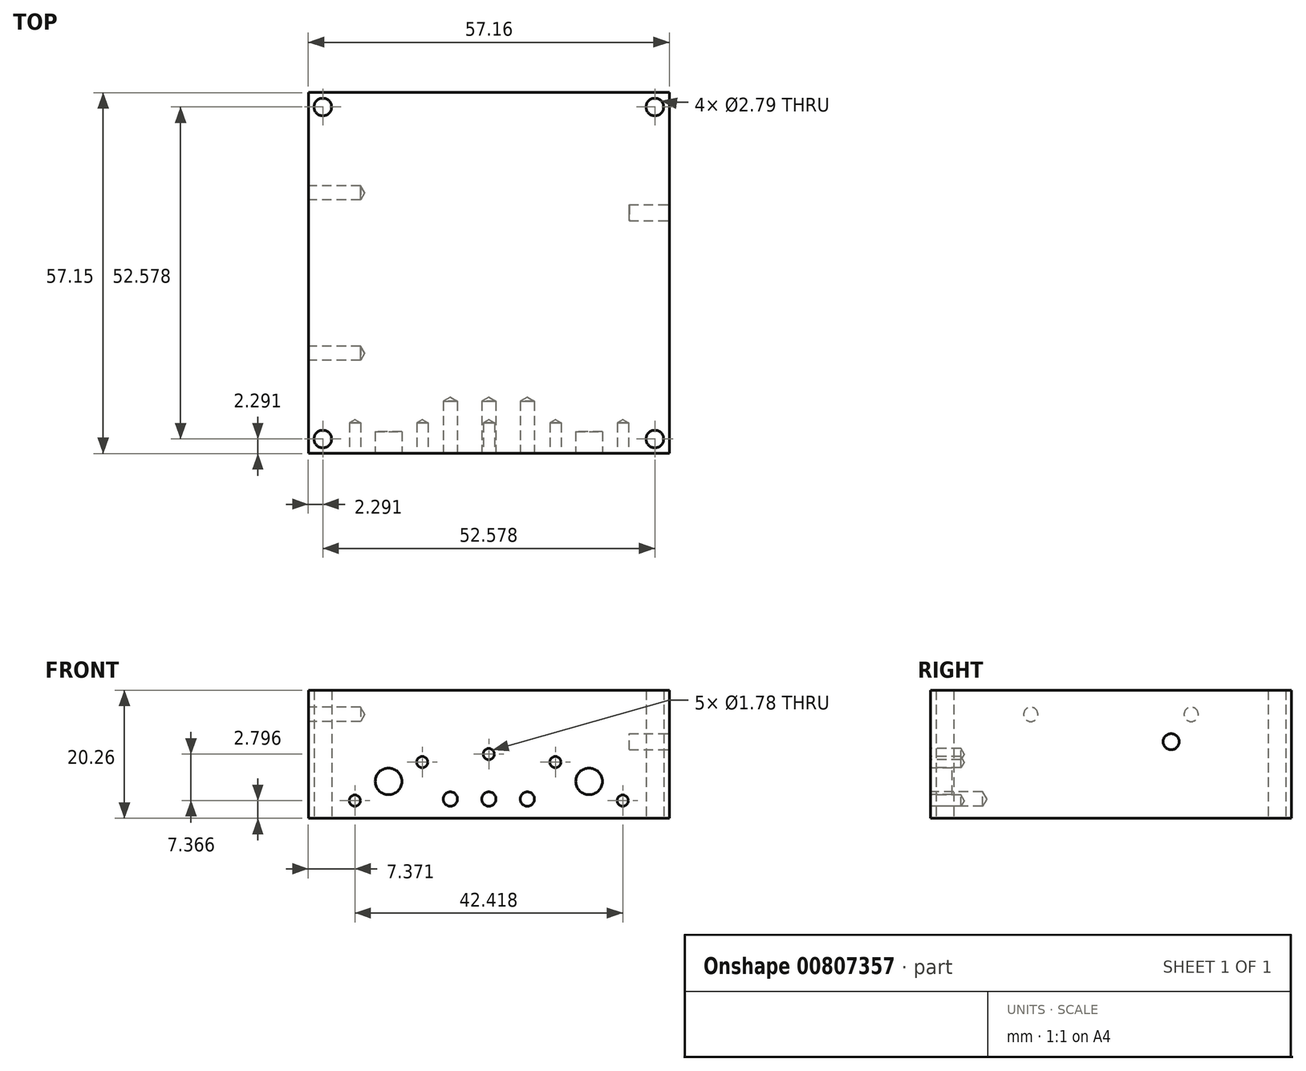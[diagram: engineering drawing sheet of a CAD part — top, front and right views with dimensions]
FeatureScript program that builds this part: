
annotation { "Feature Type Name" : "Feature", "Feature Type Description" : "" }
export const myFeature = defineFeature(function(context is Context, id is Id, definition is map)
    precondition{}
    {
        {
            var Q0;
            Q0=qCreatedBy(makeId("Top.planeOp"),FACE);
            var sketch = newSketch(context, id + "F0", { "sketchPlane" : qUnion([Q0])});
            skLineSegment(sketch, "E0.bottom", {"start": v(-28.57, 28.57) * mm, "end": v(28.58, 28.57) * mm});
            skLineSegment(sketch, "E0.top", {"start": v(-28.58, -28.58) * mm, "end": v(28.58, -28.58) * mm});
            skLineSegment(sketch, "E0.left", {"start": v(-28.57, 28.57) * mm, "end": v(-28.58, -28.58) * mm});
            skLineSegment(sketch, "E0.right", {"start": v(28.58, 28.57) * mm, "end": v(28.58, -28.57) * mm});
            skLineSegment(sketch, "E1", {"start": v(-28.58, -28.58) * mm, "end": v(28.58, 28.58) * mm, "construction": true});
            skSolve(sketch);
        }
        {
            var Q0;
            Q0 = qSketchRegion(id + "F0", true);
            extrude(context, id + "F1", {"entities" : qUnion([Q0]), "endBound" : BoundingType.SYMMETRIC, "depth" : 20.26 * mm, "offsetDistance" : 25.4 * mm});
        }
        {
            var Q0;
            Q0=makeQuery(id+"F1.opExtrude","SWEPT_FACE",FACE,{"disambiguationData":[OSD([sQuery(id+"F0.wireOp",EDGE,"E0.top")])]});
            var sketch = newSketch(context, id + "F2", { "sketchPlane" : qUnion([Q0])});
            skCircle(sketch, "E2", {"center": v(-15.88, -4.29) * mm, "radius": 2.1 * mm});
            skCircle(sketch, "E3", {"center": v(15.88, -4.29) * mm, "radius": 2.1 * mm});
            skSolve(sketch);
        }
        {
            var Q0;
            Q0 = qSketchRegion(id + "F2", true);
            extrude(context, id + "F3", {"entities" : qUnion([Q0]), "operationType" : NewBodyOperationType.REMOVE, "oppositeDirection" : true, "depth" : 3.43 * mm, "offsetDistance" : 25.4 * mm});
        }
        {
            var Q0;
            Q0=makeQuery(id+"F1.opExtrude","SWEPT_FACE",FACE,{"disambiguationData":[OSD([sQuery(id+"F0.wireOp",EDGE,"E0.top")])]});
            var sketch = newSketch(context, id + "F4", { "sketchPlane" : qUnion([Q0])});
            skCircle(sketch, "E4", {"center": v(-21.2, -7.33) * mm, "radius": 0.18 * mm});
            skCircle(sketch, "E5", {"center": v(-10.54, -1.24) * mm, "radius": 0.18 * mm});
            skLineSegment(sketch, "E6", {"start": v(0, 10.13) * mm, "end": v(0, -10.13) * mm, "construction": true});
            skCircle(sketch, "E7.MirrorC", {"center": v(10.54, -1.24) * mm, "radius": 0.18 * mm});
            skCircle(sketch, "E8.MirrorC", {"center": v(21.2, -7.33) * mm, "radius": 0.18 * mm});
            skLineSegment(sketch, "E9", {"start": v(-15.88, -4.29) * mm, "end": v(-15.88, -10.13) * mm, "construction": true});
            skLineSegment(sketch, "E10", {"start": v(-15.88, -10.13) * mm, "end": v(-15.88, -4.29) * mm, "construction": true});
            skLineSegment(sketch, "E11", {"start": v(-28.58, -4.29) * mm, "end": v(-15.88, -4.29) * mm, "construction": true});
            skLineSegment(sketch, "E12", {"start": v(-15.91, -4.3) * mm, "end": v(-21.2, -7.33) * mm, "construction": true});
            skSolve(sketch);
        }
        {
            var Q0;
            Q0=makeQuery(id+"F1.opExtrude","CAP_FACE",FACE,{"disambiguationData":[OSD([sQuery(id+"F0.wireOp",EDGE,"E0.bottom"),sQuery(id+"F0.wireOp",EDGE,"E0.top"),sQuery(id+"F0.wireOp",EDGE,"E0.left"),sQuery(id+"F0.wireOp",EDGE,"E0.right")])],"isStart":true});
            var sketch = newSketch(context, id + "F5", { "sketchPlane" : qUnion([Q0])});
            skCircle(sketch, "E13", {"center": v(-26.29, 26.29) * mm, "radius": 1.4 * mm});
            skLineSegment(sketch, "E14", {"start": v(0, 28.58) * mm, "end": v(0, -28.57) * mm, "construction": true});
            skLineSegment(sketch, "E15", {"start": v(-28.57, 0) * mm, "end": v(28.58, 0) * mm, "construction": true});
            skCircle(sketch, "E16.MirrorC", {"center": v(26.29, 26.29) * mm, "radius": 1.4 * mm});
            skCircle(sketch, "E17.MirrorC", {"center": v(26.29, -26.29) * mm, "radius": 1.4 * mm});
            skCircle(sketch, "E18.MirrorC", {"center": v(-26.29, -26.29) * mm, "radius": 1.4 * mm});
            skSolve(sketch);
        }
        {
            var Q0;
            Q0 = qSketchRegion(id + "F5", true);
            extrude(context, id + "F6", {"entities" : qUnion([Q0]), "operationType" : NewBodyOperationType.REMOVE, "endBound" : BoundingType.THROUGH_ALL, "oppositeDirection" : true, "depth" : 25.4 * mm, "offsetDistance" : 25.4 * mm});
        }
        {
            var Q0;
            Q0=makeQuery(id+"F1.opExtrude","SWEPT_FACE",FACE,{"disambiguationData":[OSD([sQuery(id+"F0.wireOp",EDGE,"E0.left")])]});
            var sketch = newSketch(context, id + "F7", { "sketchPlane" : qUnion([Q0])});
            skPoint(sketch, "E19", {"position": v(12.7, 6.32) * mm});
            skLineSegment(sketch, "E20", {"start": v(0, 10.13) * mm, "end": v(0, -10.13) * mm, "construction": true});
            skPoint(sketch, "E21.MirrorP", {"position": v(-12.7, 6.32) * mm});
            skSolve(sketch);
        }
        {
            var Q0;
            Q0=sQuery(id+"F7.wireOp",VERTEX,"E19");
            var Q1;
            Q1=sQuery(id+"F7.wireOp",VERTEX,"E21.MirrorP");
            var Q2;
            Q2=makeQuery(id+"F1.opExtrude","SWEPT_BODY",BODY,{"disambiguationData":[OSD([sQuery(id+"F0.wireOp",EDGE,"E0.bottom"),sQuery(id+"F0.wireOp",EDGE,"E0.top"),sQuery(id+"F0.wireOp",EDGE,"E0.left"),sQuery(id+"F0.wireOp",EDGE,"E0.right")])]});
            hole(context, id + "F8", {"style" : HoleStyle.SIMPLE, "endStyle" : HoleEndStyle.BLIND, "standardTappedOrClearance" : lookupTablePath({ "standard" : "ANSI", "engagement" : "75%", "pitch" : "40 tpi", "size" : "#4", "type" : "Tapped" }), "standardBlindInLast" : lookupTablePath({ "standard" : "ANSI", "engagement" : "75%", "pitch" : "40 tpi", "size" : "#4", "type" : "Tapped" }), "holeDiameter" : 2.26 * mm, "majorDiameter" : 2.84 * mm, "showTappedDepth" : true, "holeDepth" : 8.27 * mm, "tappedDepth" : 6.36 * mm, "tapClearance" : 3, "locations" : qUnion([Q0, Q1]), "scope" : qUnion([Q2])});
        }
        {
            var Q0;
            Q0=makeQuery(id+"F1.opExtrude","SWEPT_FACE",FACE,{"disambiguationData":[OSD([sQuery(id+"F0.wireOp",EDGE,"E0.right")])]});
            var sketch = newSketch(context, id + "F9", { "sketchPlane" : qUnion([Q0])});
            skCircle(sketch, "E22", {"center": v(9.53, 2) * mm, "radius": 1.27 * mm});
            skSolve(sketch);
        }
        {
            var Q0;
            Q0 = qSketchRegion(id + "F9", true);
            extrude(context, id + "F10", {"entities" : qUnion([Q0]), "operationType" : NewBodyOperationType.REMOVE, "oppositeDirection" : true, "depth" : 6.35 * mm, "offsetDistance" : 25.4 * mm});
        }
        {
            var Q0;
            Q0=makeQuery(id+"F1.opExtrude","SWEPT_FACE",FACE,{"disambiguationData":[OSD([sQuery(id+"F0.wireOp",EDGE,"E0.top")])]});
            var sketch = newSketch(context, id + "F11", { "sketchPlane" : qUnion([Q0])});
            skPoint(sketch, "E23", {"position": v(-6.1, -7.08) * mm});
            skPoint(sketch, "E24", {"position": v(0, -7.08) * mm});
            skPoint(sketch, "E25", {"position": v(6.1, -7.08) * mm});
            skSolve(sketch);
        }
        {
            var Q0;
            Q0=sQuery(id+"F11.wireOp",VERTEX,"E23");
            var Q1;
            Q1=sQuery(id+"F11.wireOp",VERTEX,"E24");
            var Q2;
            Q2=sQuery(id+"F11.wireOp",VERTEX,"E25");
            var Q3;
            Q3=makeQuery(id+"F1.opExtrude","SWEPT_BODY",BODY,{"disambiguationData":[OSD([sQuery(id+"F0.wireOp",EDGE,"E0.bottom"),sQuery(id+"F0.wireOp",EDGE,"E0.top"),sQuery(id+"F0.wireOp",EDGE,"E0.left"),sQuery(id+"F0.wireOp",EDGE,"E0.right")])]});
            hole(context, id + "F12", {"style" : HoleStyle.SIMPLE, "endStyle" : HoleEndStyle.BLIND, "standardTappedOrClearance" : lookupTablePath({ "standard" : "ANSI", "engagement" : "75%", "pitch" : "40 tpi", "size" : "#4", "type" : "Tapped" }), "standardBlindInLast" : lookupTablePath({ "standard" : "ANSI", "engagement" : "75%", "pitch" : "40 tpi", "size" : "#4", "type" : "Tapped" }), "holeDiameter" : 2.26 * mm, "majorDiameter" : 2.84 * mm, "showTappedDepth" : true, "holeDepth" : 8.26 * mm, "isTappedThrough" : true, "tappedDepth" : 6.35 * mm, "tapClearance" : 3, "locations" : qUnion([Q0, Q1, Q2]), "scope" : qUnion([Q3])});
        }
        {
            var Q0;
            Q0=makeQuery(id+"F1.opExtrude","SWEPT_FACE",FACE,{"disambiguationData":[OSD([sQuery(id+"F0.wireOp",EDGE,"E0.top")])]});
            var sketch = newSketch(context, id + "F13", { "sketchPlane" : qUnion([Q0])});
            skPoint(sketch, "E26", {"position": v(0, 0.03) * mm});
            skSolve(sketch);
        }
        {
            var Q0;
            Q0=sQuery(id+"F4.wireOp",VERTEX,"E12.end");
            var Q1;
            Q1=sQuery(id+"F4.wireOp",VERTEX,"E5.center");
            var Q2;
            Q2=sQuery(id+"F4.wireOp",VERTEX,"E7.MirrorC.center");
            var Q3;
            Q3=sQuery(id+"F4.wireOp",VERTEX,"E8.MirrorC.center");
            var Q4;
            Q4=sQuery(id+"F13.wireOp",VERTEX,"E26");
            var Q5;
            Q5=makeQuery(id+"F1.opExtrude","SWEPT_BODY",BODY,{"disambiguationData":[OSD([sQuery(id+"F0.wireOp",EDGE,"E0.bottom"),sQuery(id+"F0.wireOp",EDGE,"E0.top"),sQuery(id+"F0.wireOp",EDGE,"E0.left"),sQuery(id+"F0.wireOp",EDGE,"E0.right")])]});
            hole(context, id + "F14", {"style" : HoleStyle.SIMPLE, "endStyle" : HoleEndStyle.BLIND, "standardTappedOrClearance" : lookupTablePath({ "standard" : "ANSI", "engagement" : "75%", "pitch" : "56 tpi", "size" : "#2", "type" : "Tapped" }), "standardBlindInLast" : lookupTablePath({ "standard" : "ANSI", "engagement" : "75%", "pitch" : "56 tpi", "size" : "#2", "type" : "Tapped" }), "holeDiameter" : 1.78 * mm, "majorDiameter" : 2.18 * mm, "showTappedDepth" : true, "holeDepth" : 4.83 * mm, "isTappedThrough" : true, "tappedDepth" : 3.47 * mm, "tapClearance" : 3, "locations" : qUnion([Q0, Q1, Q2, Q3, Q4]), "scope" : qUnion([Q5])});
        }
    });
